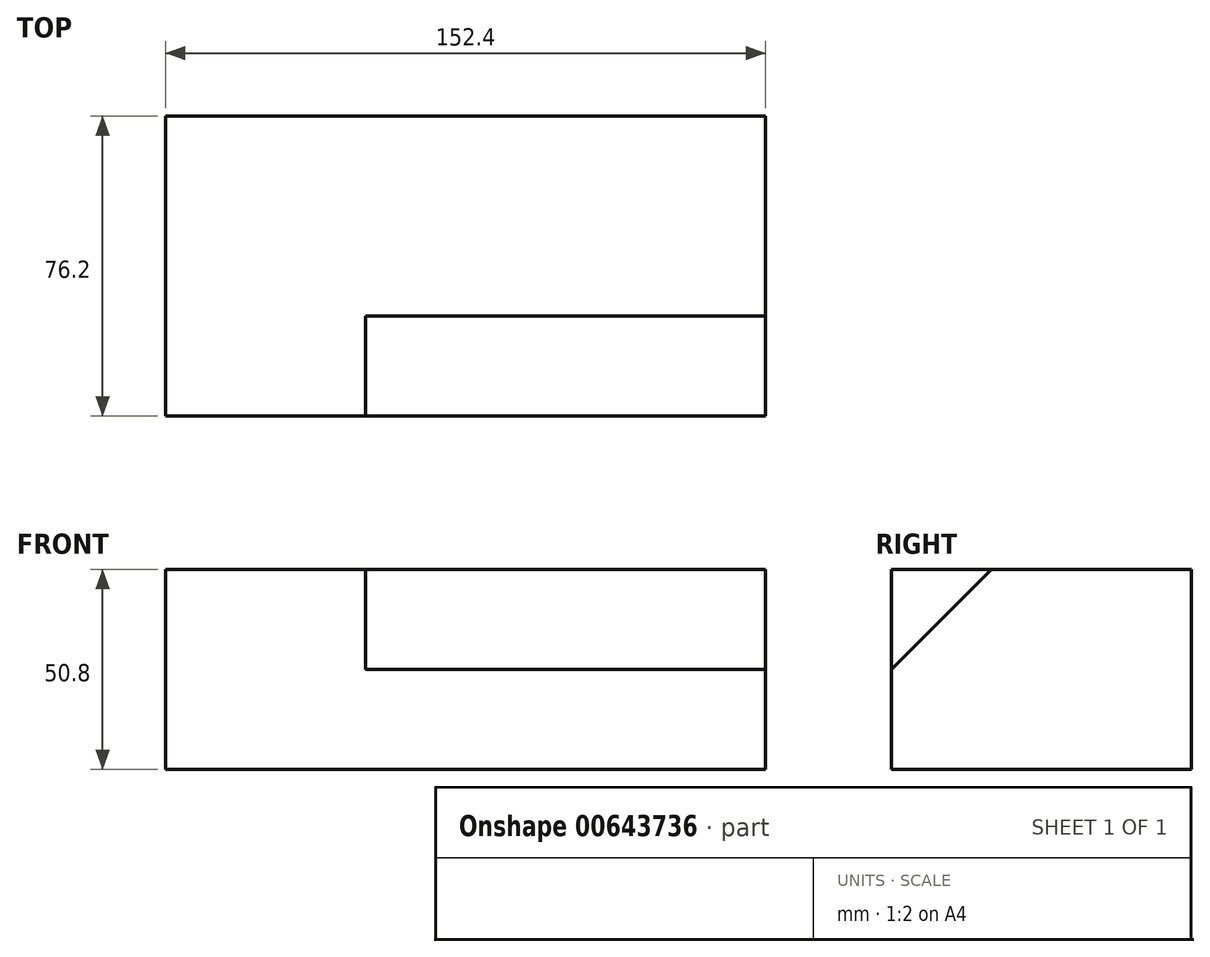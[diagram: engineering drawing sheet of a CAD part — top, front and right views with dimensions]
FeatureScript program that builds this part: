
annotation { "Feature Type Name" : "Feature", "Feature Type Description" : "" }
export const myFeature = defineFeature(function(context is Context, id is Id, definition is map)
    precondition{}
    {
        {
            var Q0;
            Q0=qCreatedBy(makeId("Right.planeOp"),FACE);
            var sketch = newSketch(context, id + "F0", { "sketchPlane" : qUnion([Q0])});
            skLineSegment(sketch, "E0.bottom", {"start": v(-63.84, 109.16) * mm, "end": v(12.36, 109.16) * mm});
            skLineSegment(sketch, "E0.top", {"start": v(-63.84, 58.36) * mm, "end": v(12.36, 58.36) * mm});
            skLineSegment(sketch, "E0.left", {"start": v(-63.84, 109.16) * mm, "end": v(-63.84, 58.36) * mm});
            skLineSegment(sketch, "E0.right", {"start": v(12.36, 109.16) * mm, "end": v(12.36, 58.36) * mm});
            skLineSegment(sketch, "E1", {"start": v(-86.55, -97.57) * mm, "end": v(-30.54, -99.08) * mm});
            skLineSegment(sketch, "E2", {"start": v(-63.84, 58.36) * mm, "end": v(-63.84, 83.76) * mm});
            skLineSegment(sketch, "E3", {"start": v(-38.44, 109.16) * mm, "end": v(12.36, 109.16) * mm});
            skLineSegment(sketch, "E4", {"start": v(-38.44, 109.16) * mm, "end": v(-63.84, 83.76) * mm});
            skSolve(sketch);
        }
        {
            var Q0;
            Q0=makeQuery(id+"F0.imprint","IMPRINT",FACE,{"disambiguationData":[TD([[makeQuery(id+"F0.imprint","IMPRINT",EDGE,{"derivedFrom":sQuery(id+"F0.wireOp",EDGE,"E0.top")}),1.0]])]});
            extrude(context, id + "F1", {"entities" : qUnion([Q0]), "depth" : 152.4 * mm, "offsetDistance" : 25.4 * mm});
        }
        {
            var Q0;
            Q0=makeQuery(id+"F0.imprint","IMPRINT",FACE,{"disambiguationData":[TD([[makeQuery(id+"F0.imprint","IMPRINT",EDGE,{"derivedFrom":sQuery(id+"F0.wireOp",EDGE,"E0.bottom")}),-1.0]])]});
            extrude(context, id + "F2", {"entities" : qUnion([Q0]), "operationType" : NewBodyOperationType.ADD, "depth" : 50.8 * mm, "offsetDistance" : 25.4 * mm});
        }
    });
